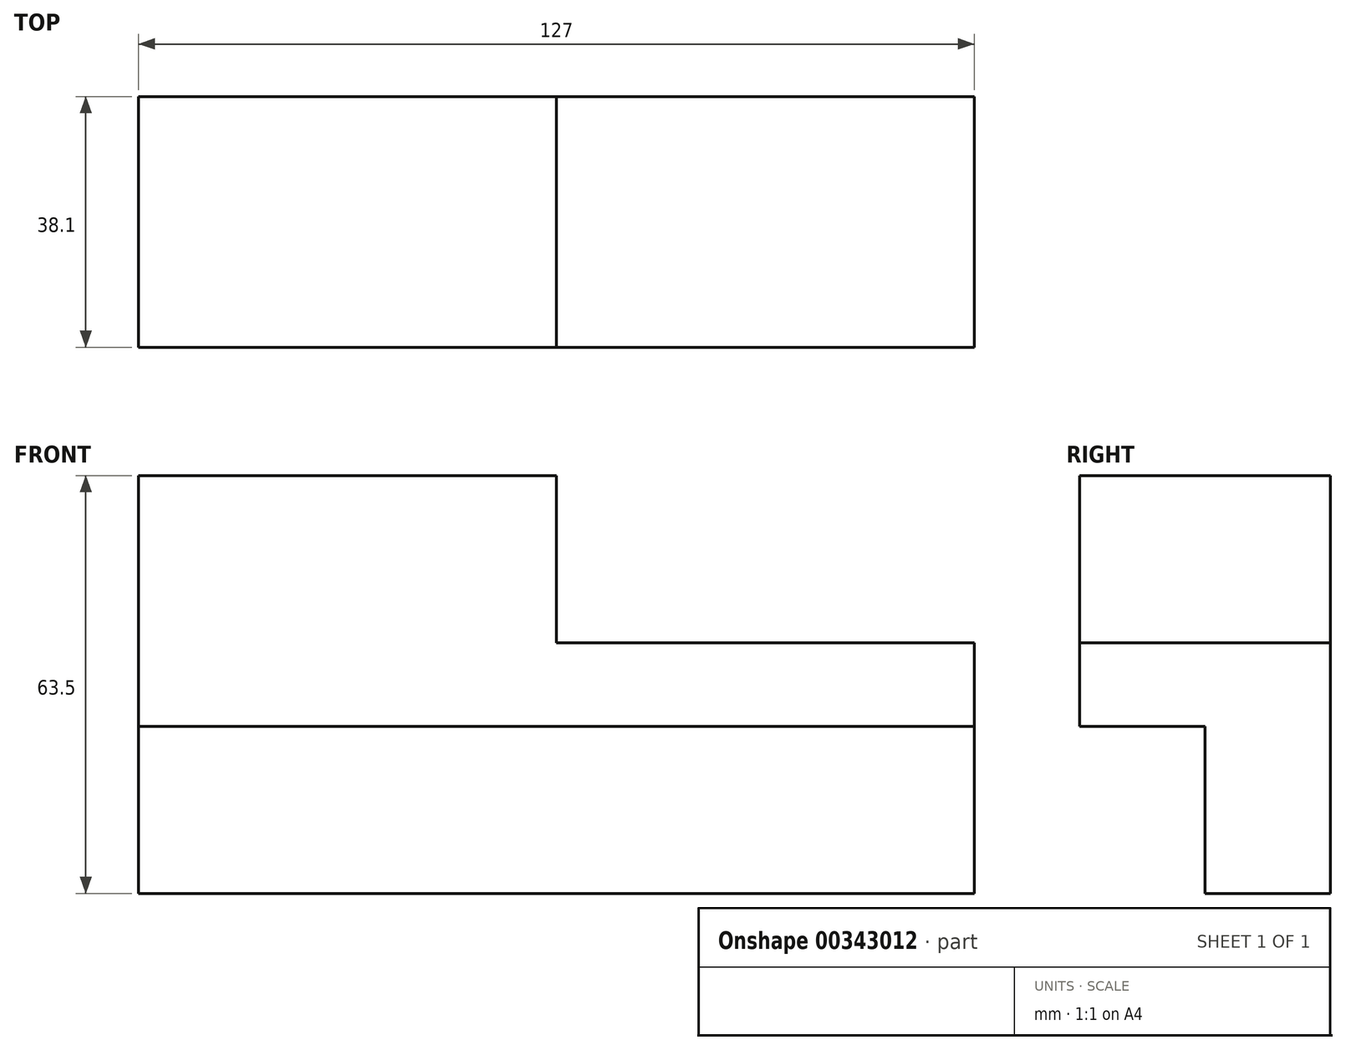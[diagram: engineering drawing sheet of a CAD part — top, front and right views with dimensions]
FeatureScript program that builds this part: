
annotation { "Feature Type Name" : "Feature", "Feature Type Description" : "" }
export const myFeature = defineFeature(function(context is Context, id is Id, definition is map)
    precondition{}
    {
        {
            var Q0;
            Q0=qCreatedBy(makeId("Front.planeOp"),FACE);
            var sketch = newSketch(context, id + "F0", { "sketchPlane" : qUnion([Q0])});
            skLineSegment(sketch, "E0", {"start": v(63.5, -27.84) * mm, "end": v(-63.5, -27.84) * mm});
            skLineSegment(sketch, "E1", {"start": v(-63.5, -27.84) * mm, "end": v(-63.5, 35.66) * mm});
            skLineSegment(sketch, "E2", {"start": v(-63.5, 35.66) * mm, "end": v(0, 35.66) * mm});
            skLineSegment(sketch, "E3", {"start": v(0, 35.66) * mm, "end": v(0, 10.26) * mm});
            skLineSegment(sketch, "E4", {"start": v(0, 10.26) * mm, "end": v(63.5, 10.26) * mm});
            skLineSegment(sketch, "E5", {"start": v(63.5, 10.26) * mm, "end": v(63.5, -27.84) * mm});
            skLineSegment(sketch, "E6", {"start": v(63.5, -27.84) * mm, "end": v(63.5, -2.44) * mm});
            skLineSegment(sketch, "E7", {"start": v(63.5, -2.44) * mm, "end": v(-63.5, -2.44) * mm});
            skSolve(sketch);
        }
        {
            var Q0;
            {var subQ0=sQuery(id+"F0.wireOp",EDGE,"E2");Q0=makeQuery(id+"F0.imprint","IMPRINT",FACE,{"disambiguationData":[TD([[makeQuery(id+"F0.imprint","IMPRINT",EDGE,{"derivedFrom":subQ0}),-1.0]])]});}
            extrude(context, id + "F1", {"entities" : qUnion([Q0]), "depth" : 38.1 * mm});
        }
        {
            var Q0;
            {var subQ0=sQuery(id+"F0.wireOp",EDGE,"E0");Q0=makeQuery(id+"F0.imprint","IMPRINT",FACE,{"disambiguationData":[TD([[makeQuery(id+"F0.imprint","IMPRINT",EDGE,{"derivedFrom":subQ0}),-1.0]])]});}
            extrude(context, id + "F2", {"entities" : qUnion([Q0]), "operationType" : NewBodyOperationType.ADD, "depth" : 19.05 * mm});
        }
    });
